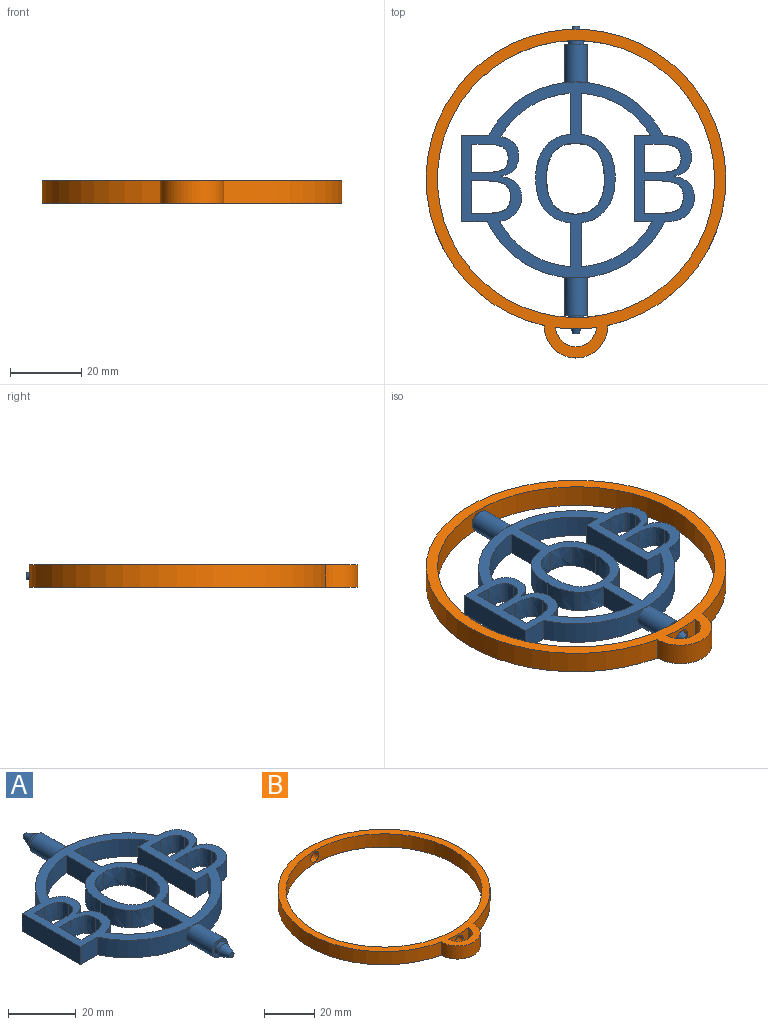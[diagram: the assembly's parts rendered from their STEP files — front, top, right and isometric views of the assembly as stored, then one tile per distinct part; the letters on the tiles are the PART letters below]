
ASSEMBLY  parts=2 mates=1
PART A: 91 faces, bbox 65.3x86.4x6.4 mm
  f0: cylinder r=27.5mm len=24.86mm, axis (0,0,1), area 181.3mm2, adj f34,f44,f45,f83
  f1: cylinder r=27.5mm len=24.5mm, axis (0,0,1), area 176.1mm2, adj f42,f44,f45,f82
  f2: extruded ~6.35x6.06mm, area 43.2mm2, adj f8,f44,f45,f75
  f3: extruded ~6.35x6.09mm, area 43.4mm2, adj f10,f44,f45,f76
  f4: cylinder r=24.36mm len=19.45mm, axis (0,0,1), area 151.6mm2, adj f19,f44,f45,f72
  f5: cylinder r=24.36mm len=19.84mm, axis (0,0,1), area 156.2mm2, adj f6,f18,f44,f45
  f6: plane 12.28x6.35mm, normal (-1,0,0), area 78mm2, adj f5,f9,f44,f45
  f7: extruded ~6.76x6.35mm, area 48.6mm2, adj f44,f45,f72,f79
  f8: extruded ~6.35x6.13mm, area 43.6mm2, adj f2,f44,f45,f74
  f9: extruded ~6.82x6.35mm, area 49.1mm2, adj f6,f44,f45,f80
  f10: extruded ~6.35x6.1mm, area 43.4mm2, adj f3,f44,f45,f73
  f11: cylinder r=24.36mm len=19.75mm, axis (0,0,1), area 155mm2, adj f15,f44,f45,f47
  f12: cylinder r=27.5mm len=24.86mm, axis (0,0,1), area 181.3mm2, adj f44,f45,f62,f83
  f13: cylinder r=24.36mm len=19.42mm, axis (0,0,1), area 150.2mm2, adj f44,f45,f60,f71
  f14: cylinder r=27.5mm len=24.51mm, axis (0,0,1), area 176.2mm2, adj f44,f45,f46,f82
  f15: plane 12.32x6.35mm, normal (1,0,0), area 78.2mm2, adj f11,f16,f44,f45
  f16: extruded ~6.46x6.35mm, area 47mm2, adj f15,f44,f45,f77
  f17: extruded ~6.52x6.35mm, area 47.3mm2, adj f44,f45,f71,f78
  f18: extruded ~6.35x3.96mm, area 27.6mm2, adj f5,f35,f44,f45
  f19: extruded ~6.35x2.89mm, area 19.7mm2, adj f4,f40,f44,f45
  f20: plane 9.08x6.35mm, normal (1,0,0), area 57.6mm2, adj f21,f43,f44,f45
  f21: plane 6.35x4.83mm, normal (0,-1,0), area 30.7mm2, adj f20,f22,f44,f45
  f22: extruded ~6.35x4.62mm, area 30.5mm2, adj f21,f23,f44,f45
  f23: extruded ~6.35x3.32mm, area 24.2mm2, adj f22,f24,f44,f45
  f24: extruded ~6.35x3.56mm, area 25.4mm2, adj f23,f25,f44,f45
  f25: extruded ~6.35x4.42mm, area 29.5mm2, adj f24,f43,f44,f45
  f26: plane 6.35x4.64mm, normal (0,1,0), area 29.5mm2, adj f27,f41,f44,f45
  f27: plane 7.94x6.35mm, normal (1,0,0), area 50.4mm2, adj f26,f28,f44,f45
  f28: plane 6.35x4.15mm, normal (0,-1,0), area 26.4mm2, adj f27,f29,f44,f45
  f29: extruded ~6.35x4.64mm, area 30.4mm2, adj f28,f30,f44,f45
  f30: extruded ~6.35x2.95mm, area 21.9mm2, adj f29,f31,f44,f45
  f31: extruded ~6.35x3.16mm, area 22.6mm2, adj f30,f41,f44,f45
  f32: plane 6.85x6.35mm, normal (0,1,0), area 43.5mm2, adj f33,f42,f44,f45
  f33: plane 24.25x6.35mm, normal (-1,0,0), area 154mm2, adj f32,f34,f44,f45
  f34: plane 7.21x6.35mm, normal (0,-1,0), area 45.8mm2, adj f0,f33,f44,f45
  f35: extruded ~6.35x5.07mm, area 36.4mm2, adj f18,f36,f44,f45
  f36: extruded ~6.35x5.81mm, area 56.4mm2, adj f35,f37,f44,f45
  f37: plane 6.35x0.16mm, normal (1,0,0), area 1mm2, adj f36,f38,f44,f45
  f38: extruded ~6.35x3.51mm, area 25.6mm2, adj f37,f39,f44,f45
  f39: extruded ~6.35x3.56mm, area 24.4mm2, adj f38,f40,f44,f45
  f40: extruded ~6.35x4.56mm, area 33.5mm2, adj f19,f39,f44,f45
  f41: extruded ~6.35x4.3mm, area 28.4mm2, adj f26,f31,f44,f45
  f42: extruded ~6.35x0.72mm, area 4.6mm2, adj f1,f32,f44,f45
  f43: plane 6.35x5.06mm, normal (0,1,0), area 32.2mm2, adj f20,f25,f44,f45
  f44: plane 65.27x54.99mm, normal (0,0,1), area 1015.6mm2, adj f0,f1,f2,f3,f4,f5,f6,f7
  f45: plane 65.27x54.99mm, normal (0,0,-1), area 1015.6mm2, adj f0,f1,f2,f3,f4,f5,f6,f7
  f46: extruded ~6.35x5.72mm, area 37.9mm2, adj f14,f44,f45,f68
  f47: plane 6.35x4.94mm, normal (0,-1,0), area 31.4mm2, adj f11,f44,f45,f61
  f48: plane 9.08x6.35mm, normal (1,0,0), area 57.6mm2, adj f44,f45,f49,f70
  f49: plane 6.35x4.83mm, normal (0,-1,0), area 30.7mm2, adj f44,f45,f48,f50
  f50: extruded ~6.35x4.62mm, area 30.5mm2, adj f44,f45,f49,f51
  f51: extruded ~6.35x3.32mm, area 24.2mm2, adj f44,f45,f50,f52
  f52: extruded ~6.35x3.56mm, area 25.4mm2, adj f44,f45,f51,f53
  f53: extruded ~6.35x4.42mm, area 29.5mm2, adj f44,f45,f52,f70
  f54: plane 6.35x4.64mm, normal (0,1,0), area 29.5mm2, adj f44,f45,f55,f69
  f55: plane 7.94x6.35mm, normal (1,0,0), area 50.4mm2, adj f44,f45,f54,f56
  f56: plane 6.35x4.15mm, normal (0,-1,0), area 26.4mm2, adj f44,f45,f55,f57
  f57: extruded ~6.35x4.64mm, area 30.4mm2, adj f44,f45,f56,f58
  f58: extruded ~6.35x2.95mm, area 21.9mm2, adj f44,f45,f57,f59
  f59: extruded ~6.35x3.16mm, area 22.6mm2, adj f44,f45,f58,f69
  f60: plane 6.35x4.52mm, normal (0,1,0), area 28.7mm2, adj f13,f44,f45,f61
  f61: plane 24.25x6.35mm, normal (-1,0,0), area 154mm2, adj f44,f45,f47,f60
  f62: extruded ~6.35x6.15mm, area 41.5mm2, adj f12,f44,f45,f63
  f63: extruded ~6.35x5.07mm, area 36.4mm2, adj f44,f45,f62,f64
  f64: extruded ~6.35x5.81mm, area 56.4mm2, adj f44,f45,f63,f65
  f65: plane 6.35x0.16mm, normal (1,0,0), area 1mm2, adj f44,f45,f64,f66
  f66: extruded ~6.35x3.51mm, area 25.6mm2, adj f44,f45,f65,f67
  f67: extruded ~6.35x3.56mm, area 24.4mm2, adj f44,f45,f66,f68
  f68: extruded ~6.35x4.56mm, area 33.5mm2, adj f44,f45,f46,f67
  f69: extruded ~6.35x4.3mm, area 28.4mm2, adj f44,f45,f54,f59
  f70: plane 6.35x5.06mm, normal (0,1,0), area 32.2mm2, adj f44,f45,f48,f53
  f71: plane 11.53x6.35mm, normal (1,0,0), area 73.2mm2, adj f13,f17,f44,f45
  f72: plane 11.5x6.35mm, normal (-1,0,0), area 73mm2, adj f4,f7,f44,f45
  f73: extruded ~7.47x6.35mm, area 50.3mm2, adj f10,f44,f45,f74
  f74: extruded ~7.4x6.35mm, area 49.8mm2, adj f8,f44,f45,f73
  f75: extruded ~7.42x6.35mm, area 49.8mm2, adj f2,f44,f45,f76
  f76: extruded ~7.48x6.35mm, area 50.2mm2, adj f3,f44,f45,f75
  f77: extruded ~9.16x6.35mm, area 62.5mm2, adj f16,f44,f45,f78
  f78: extruded ~9.16x6.35mm, area 62.4mm2, adj f17,f44,f45,f77
  f79: extruded ~9.18x6.35mm, area 62.6mm2, adj f7,f44,f45,f80
  f80: extruded ~9.25x6.35mm, area 63mm2, adj f9,f44,f45,f79
  f81: plane 6.35x6.35mm, normal (0,1,0), area 17mm2, adj f82,f88
  f82: cylinder r=3.17mm len=10.79mm, axis (0,1,0), area 213.4mm2, adj f1,f14,f81
  f83: cylinder r=3.17mm len=10.79mm, axis (0,1,0), area 213.4mm2, adj f0,f12,f84
  f84: plane 6.35x6.35mm, normal (0,-1,0), area 17mm2, adj f83,f85
  f85: cylinder r=2.16mm len=4.32mm, axis (0,1,0), area 21.6mm2, adj f84,f87
  f86: plane 1.78x1.78mm, normal (0,-1,0), area 2.5mm2, adj f87
  f87: cone r=0.89mm half-angle=20deg, axis (0,1,0), area 35.6mm2, adj f85,f86
  f88: cylinder r=2.16mm len=4.32mm, axis (0,-1,0), area 21.6mm2, adj f81,f90
  f89: plane 1.78x1.78mm, normal (0,1,0), area 2.5mm2, adj f90
  f90: cone r=2.16mm half-angle=20deg, axis (0,-1,0), area 35.6mm2, adj f88,f89
PART B: 9 faces, bbox 84.1x92.2x6.4 mm
  f0: cylinder r=42.04mm len=11.42mm, axis (0,0,-1), area 56.3mm2, adj f3,f4,f5,f7
  f1: cylinder r=42.04mm len=84.07mm, axis (0,0,-1), area 1546.9mm2, adj f3,f4,f6,f8
  f2: cylinder r=38.86mm len=77.72mm, axis (0,0,-1), area 1517.6mm2, adj f3,f4,f5,f6
  f3: plane 92.21x84.07mm, normal (0,0,1), area 879.1mm2, adj f0,f1,f2,f7,f8
  f4: plane 92.21x84.07mm, normal (0,0,-1), area 879.1mm2, adj f0,f1,f2,f7,f8
  f5: cylinder r=2.29mm len=4.57mm, axis (0,-1,0), area 45.6mm2, adj f0,f2
  f6: cylinder r=2.29mm len=4.57mm, axis (0,-1,0), area 45.6mm2, adj f1,f2
  f7: cylinder r=5.72mm len=11.42mm, axis (0,0,1), area 109.4mm2, adj f0,f3,f4
  f8: cylinder r=8.9mm len=17.79mm, axis (0,0,1), area 179.9mm2, adj f1,f3,f4
PLACE A t=(-13.51,-1.33,3.39)mm
PLACE B t=(-13.51,-1.08,3.39)mm
MATE slider B.f5 <-> A.f85  axis (0,-1,0) through (-13.51,37.69,6.57)mm
